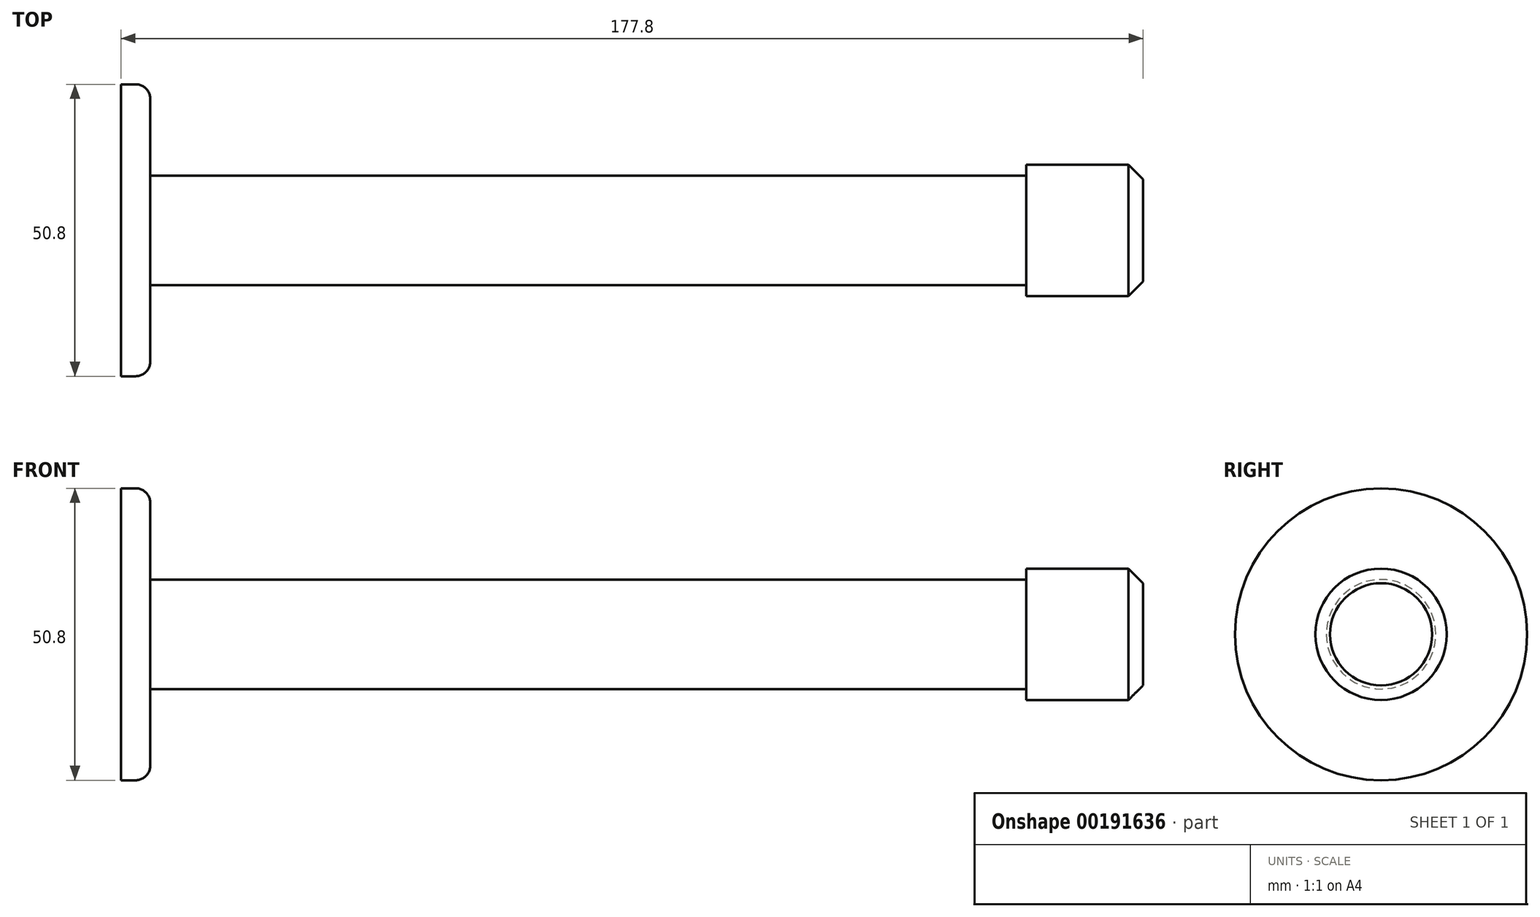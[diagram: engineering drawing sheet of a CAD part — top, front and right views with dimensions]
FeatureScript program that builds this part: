
annotation { "Feature Type Name" : "Feature", "Feature Type Description" : "" }
export const myFeature = defineFeature(function(context is Context, id is Id, definition is map)
    precondition{}
    {
        {
            var Q0;
            Q0=qCreatedBy(makeId("Right.planeOp"),FACE);
            var sketch = newSketch(context, id + "F0", { "sketchPlane" : qUnion([Q0])});
            skCircle(sketch, "E0", {"center": v(0, 0) * mm, "radius": 25.4 * mm});
            skSolve(sketch);
        }
        {
            var Q0;
            Q0=makeQuery(id+"F0.imprint","IMPRINT",FACE,{"disambiguationData":[TD([[makeQuery(id+"F0.imprint","IMPRINT",EDGE,{"derivedFrom":sQuery(id+"F0.wireOp",EDGE,"E0")}),1.0]])]});
            extrude(context, id + "F1", {"entities" : qUnion([Q0]), "depth" : 5.08 * mm});
        }
        {
            var Q0;
            Q0=makeQuery(id+"F1.opExtrude","CAP_EDGE",EDGE,{"disambiguationData":[OSD([sQuery(id+"F0.wireOp",EDGE,"E0")])],"isStart":false});
            fillet(context, id + "F2", {"entities" : qUnion([Q0]), "radius" : 2.54 * mm, "tangentPropagation" : true, "allowEdgeOverflow" : false});
        }
        {
            var Q0;
            Q0=makeQuery(id+"F1.opExtrude","CAP_FACE",FACE,{"disambiguationData":[OSD([sQuery(id+"F0.wireOp",EDGE,"E0")])],"isStart":false});
            var sketch = newSketch(context, id + "F3", { "sketchPlane" : qUnion([Q0])});
            skCircle(sketch, "E1", {"center": v(0, 0) * mm, "radius": 9.53 * mm});
            skSolve(sketch);
        }
        {
            var Q0;
            Q0 = qSketchRegion(id + "F3", true);
            extrude(context, id + "F4", {"entities" : qUnion([Q0]), "operationType" : NewBodyOperationType.ADD, "depth" : 152.4 * mm});
        }
        {
            var Q0;
            Q0=makeQuery(id+"F4.opExtrude","CAP_FACE",FACE,{"disambiguationData":[OSD([sQuery(id+"F3.wireOp",EDGE,"E1")])],"isStart":false});
            var sketch = newSketch(context, id + "F5", { "sketchPlane" : qUnion([Q0])});
            skCircle(sketch, "E2", {"center": v(0, 0) * mm, "radius": 11.43 * mm});
            skSolve(sketch);
        }
        {
            var Q0;
            Q0=makeQuery(id+"F5.imprint","IMPRINT",FACE,{"disambiguationData":[TD([[makeQuery(id+"F5.imprint","IMPRINT",EDGE,{"derivedFrom":makeQuery(id+"F4.opExtrude","CAP_EDGE",EDGE,{"disambiguationData":[OSD([sQuery(id+"F3.wireOp",EDGE,"E1")])],"isStart":false})}),1.0]])]});
            var Q1;
            Q1=makeQuery(id+"F5.imprint","IMPRINT",FACE,{"disambiguationData":[TD([[makeQuery(id+"F5.imprint","IMPRINT",EDGE,{"derivedFrom":sQuery(id+"F5.wireOp",EDGE,"E2")}),1.0]])]});
            extrude(context, id + "F6", {"entities" : qUnion([Q0, Q1]), "operationType" : NewBodyOperationType.ADD, "depth" : 20.32 * mm});
        }
        {
            var Q0;
            Q0=makeQuery(id+"F6.opExtrude","CAP_EDGE",EDGE,{"disambiguationData":[OSD([sQuery(id+"F5.wireOp",EDGE,"E2")])],"isStart":false});
            chamfer(context, id + "F7", {"entities" : qUnion([Q0]), "width" : 2.54 * mm, "tangentPropagation" : true});
        }
    });
